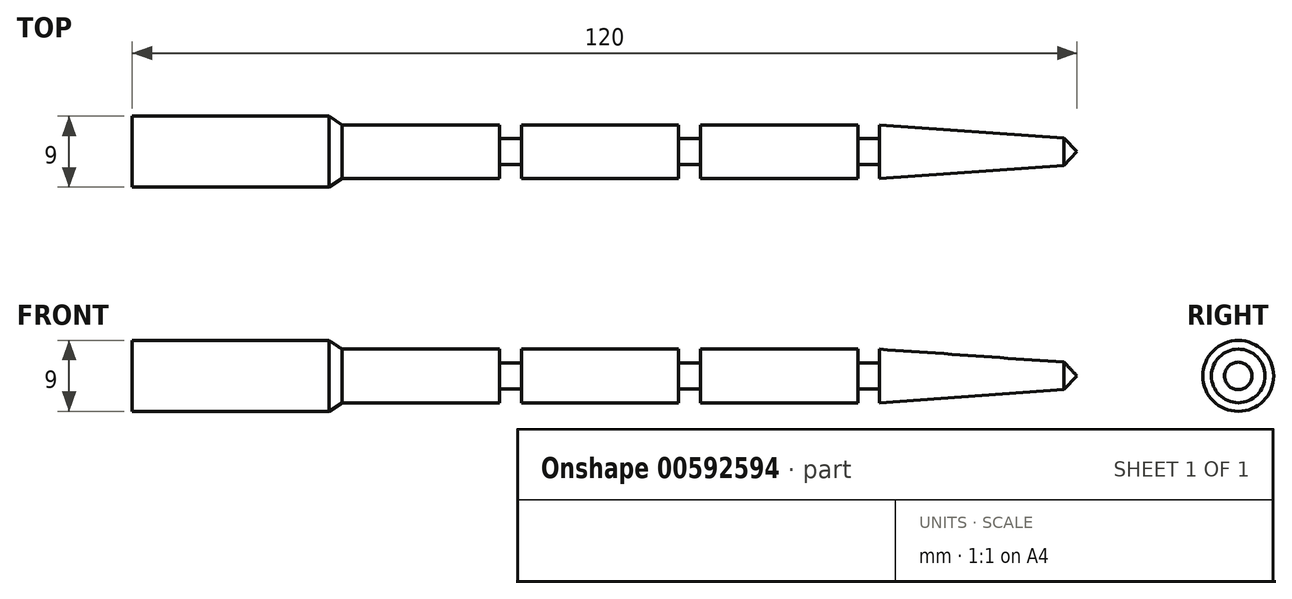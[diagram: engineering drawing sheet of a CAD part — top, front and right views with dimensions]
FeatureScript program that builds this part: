
annotation { "Feature Type Name" : "Feature", "Feature Type Description" : "" }
export const myFeature = defineFeature(function(context is Context, id is Id, definition is map)
    precondition{}
    {
        {
            var Q0;
            Q0=qCreatedBy(makeId("Front.planeOp"),FACE);
            var sketch = newSketch(context, id + "F0", { "sketchPlane" : qUnion([Q0])});
            skLineSegment(sketch, "E0", {"start": v(0, 0) * mm, "end": v(0, 4.5) * mm});
            skLineSegment(sketch, "E1", {"start": v(0, 0) * mm, "end": v(120, 0) * mm});
            skLineSegment(sketch, "E2", {"start": v(0, 4.5) * mm, "end": v(25, 4.5) * mm});
            skLineSegment(sketch, "E3", {"start": v(25, 4.5) * mm, "end": v(26.67, 3.4) * mm});
            skLineSegment(sketch, "E4", {"start": v(26.67, 3.4) * mm, "end": v(46.67, 3.4) * mm});
            skLineSegment(sketch, "E5", {"start": v(46.67, 3.4) * mm, "end": v(46.67, 1.65) * mm});
            skLineSegment(sketch, "E6", {"start": v(46.67, 1.65) * mm, "end": v(49.42, 1.65) * mm});
            skLineSegment(sketch, "E7", {"start": v(49.42, 1.65) * mm, "end": v(49.42, 3.4) * mm});
            skLineSegment(sketch, "E8", {"start": v(49.42, 3.4) * mm, "end": v(69.42, 3.4) * mm});
            skLineSegment(sketch, "E9", {"start": v(69.42, 3.4) * mm, "end": v(69.42, 1.65) * mm});
            skLineSegment(sketch, "E10", {"start": v(69.42, 1.65) * mm, "end": v(72.17, 1.65) * mm});
            skLineSegment(sketch, "E11", {"start": v(72.17, 1.65) * mm, "end": v(72.17, 3.4) * mm});
            skLineSegment(sketch, "E12", {"start": v(72.17, 3.4) * mm, "end": v(92.17, 3.4) * mm});
            skLineSegment(sketch, "E13", {"start": v(92.17, 3.4) * mm, "end": v(92.17, 1.65) * mm});
            skLineSegment(sketch, "E14", {"start": v(92.17, 1.65) * mm, "end": v(94.92, 1.65) * mm});
            skLineSegment(sketch, "E15", {"start": v(94.92, 1.65) * mm, "end": v(94.92, 3.4) * mm});
            skLineSegment(sketch, "E16", {"start": v(94.92, 3.4) * mm, "end": v(118.38, 1.74) * mm});
            skLineSegment(sketch, "E17", {"start": v(118.38, 1.74) * mm, "end": v(118.38, 0) * mm});
            skLineSegment(sketch, "E18", {"start": v(118.38, 1.74) * mm, "end": v(120, 0) * mm});
            skLineSegment(sketch, "E19", {"start": v(120, 0) * mm, "end": v(118.38, 0) * mm});
            skSolve(sketch);
        }
        {
            var Q0;
            Q0=makeQuery(id+"F0.imprint","IMPRINT",FACE,{"disambiguationData":[TD([[makeQuery(id+"F0.imprint","IMPRINT",EDGE,{"derivedFrom":sQuery(id+"F0.wireOp",EDGE,"E17")}),1.0]])]});
            var Q1;
            Q1=makeQuery(id+"F0.imprint","IMPRINT",FACE,{"disambiguationData":[TD([[makeQuery(id+"F0.imprint","IMPRINT",EDGE,{"derivedFrom":sQuery(id+"F0.wireOp",EDGE,"E0")}),-1.0]])]});
            var Q2;
            Q2=sQuery(id+"F0.wireOp",EDGE,"E1");
            revolve(context, id + "F1", {"entities" : qUnion([Q0, Q1]), "axis" : qUnion([Q2]), "revolveType" : RevolveType.FULL});
        }
    });
